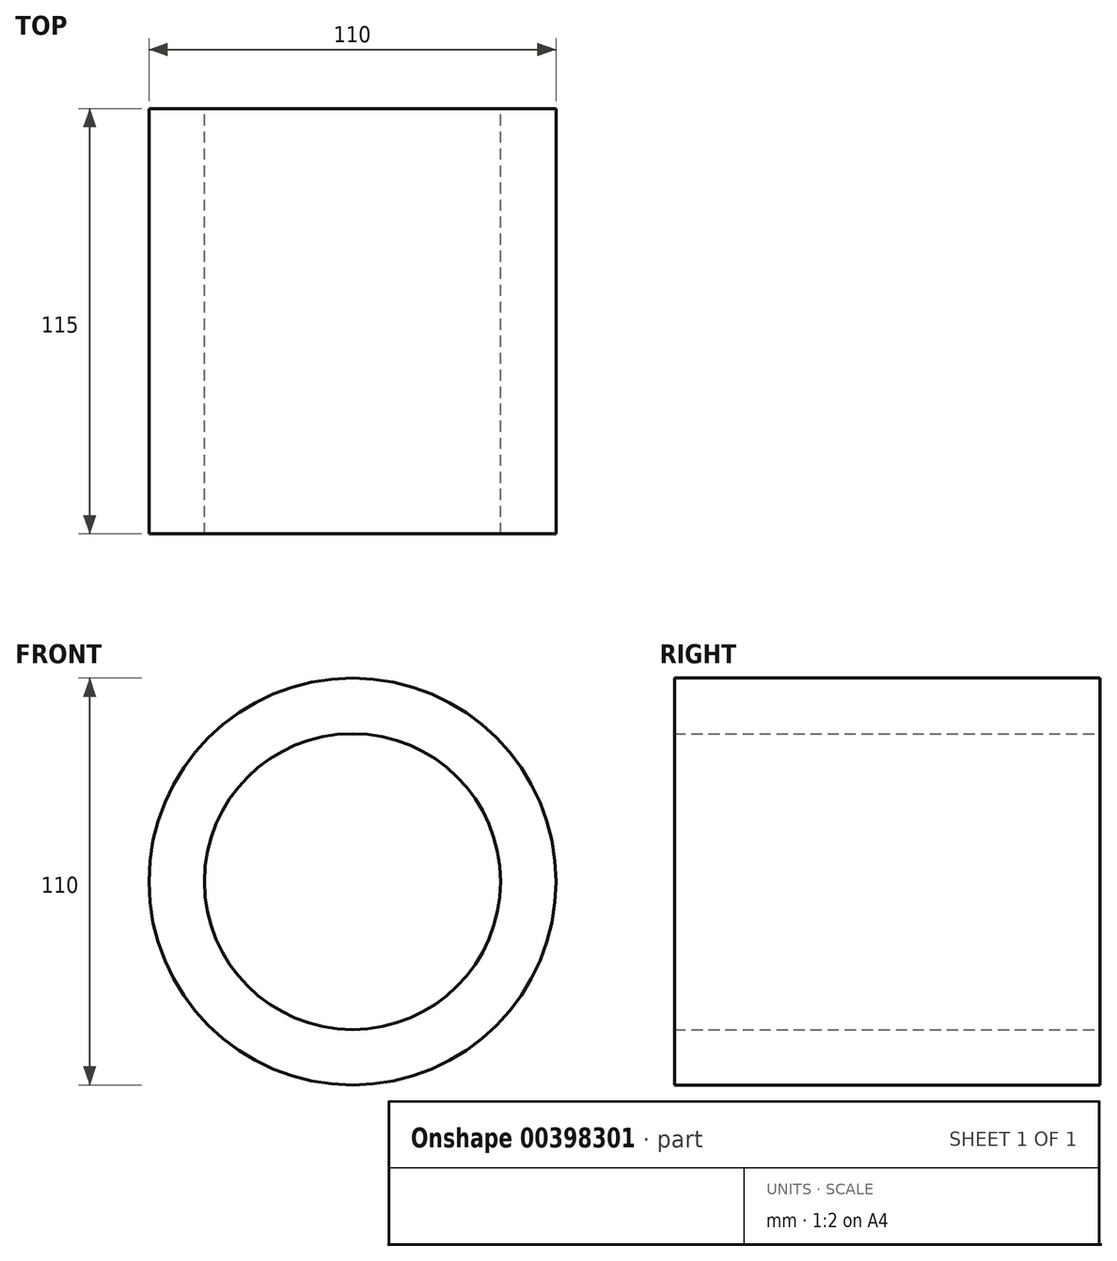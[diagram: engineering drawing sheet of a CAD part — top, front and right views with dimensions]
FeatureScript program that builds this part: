
annotation { "Feature Type Name" : "Feature", "Feature Type Description" : "" }
export const myFeature = defineFeature(function(context is Context, id is Id, definition is map)
    precondition{}
    {
        {
            var Q0;
            Q0=qCreatedBy(makeId("Front.planeOp"),FACE);
            var sketch = newSketch(context, id + "F0", { "sketchPlane" : qUnion([Q0])});
            skCircle(sketch, "E0", {"center": v(0, 0) * mm, "radius": 40 * mm});
            skCircle(sketch, "E1", {"center": v(0, 0) * mm, "radius": 55 * mm});
            skSolve(sketch);
        }
        {
            var Q0;
            Q0=makeQuery(id+"F0.imprint","IMPRINT",FACE,{"disambiguationData":[TD([[makeQuery(id+"F0.imprint","IMPRINT",EDGE,{"derivedFrom":sQuery(id+"F0.wireOp",EDGE,"E0")}),-1.0]])]});
            extrude(context, id + "F1", {"entities" : qUnion([Q0]), "depth" : 115 * mm});
        }
    });
